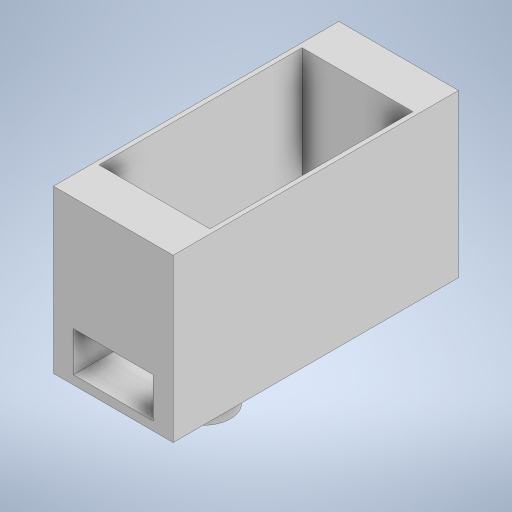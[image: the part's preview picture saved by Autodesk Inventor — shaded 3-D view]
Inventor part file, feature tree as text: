
AUTODESK INVENTOR PART (.ipt)
format: ipt  version: 2023 (Build 270158000, 158)  size: 273,408 bytes
history: native  units: mm
features: extrude x6, sketch x5
ambient origin geometry x8: Origin, YZ Plane, XZ Plane, XY Plane, X Axis, Y Axis, Z Axis, Center Point
bodies: Solid1 (feature_tree)
feature tree (11):
  sketch  "Sketch1"  dims[d0=12.5mm d1=22.9mm]
  extrude  "Extrusion1"  Depth=22.9mm
  extrude  "Extrusion2"  Depth=0.5mm
  extrude  "Extrusion3"  Depth=4.65mm
  extrude  "Extrusion4"  Depth=2.45mm
  extrude  "Extrusion7"  Depth=3.4mm
  extrude  "Extrusion8"  Depth=17.3mm TaperAngle=0.0deg
  sketch  "Sketch2"  dims[d2=0.5mm d3=0.5mm]
  sketch  "Sketch3"  dims[d4=4.65mm d5=4.65mm]
  sketch  "Sketch7"  dims[d6=2.45mm d7=2.45mm]
  sketch  "Sketch8"  dims[d8=1.5mm d9=1.5mm d10=17.3mm d11=0.0mm d12=1.0mm d13=0.0mm d18=4.7mm d19=0.0mm d20=4.65mm d21=6.7mm d22=5.6mm d23=6.05mm d24=1.385mm d25=1.385mm d26=0.32mm d27=0.32mm d28=0.64mm d30=2.77mm d31=0.64mm d32=2.77mm d33=1.2mm d34=0.0mm d47=1.0mm d48=4.5mm d49=4.5mm d50=9.0mm d51=5.5mm d52=0.0mm d53=1.7mm d54=0.37mm d55=3.4mm d56=0.74mm d57=3.4mm d58=3.0mm d59=0.0mm d60=1.7mm d61=0.37mm d62=3.4mm d63=0.74mm d64=3.4mm]
